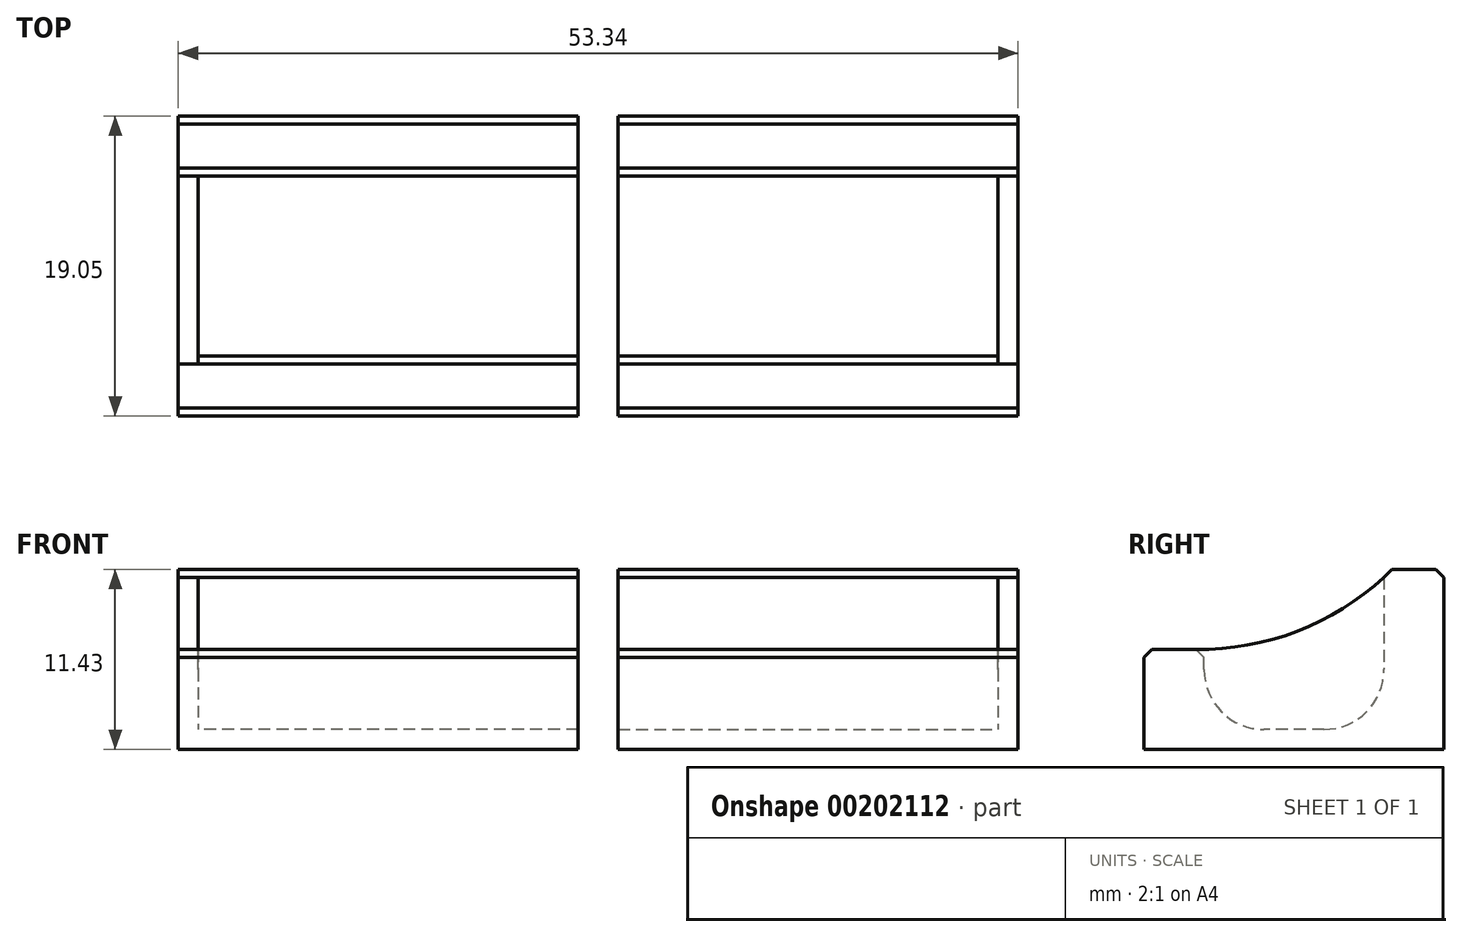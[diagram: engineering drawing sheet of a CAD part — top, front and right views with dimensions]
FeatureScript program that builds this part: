
annotation { "Feature Type Name" : "Feature", "Feature Type Description" : "" }
export const myFeature = defineFeature(function(context is Context, id is Id, definition is map)
    precondition{}
    {
        {
            var Q0;
            Q0=qCreatedBy(makeId("Right.planeOp"),FACE);
            var sketch = newSketch(context, id + "F0", { "sketchPlane" : qUnion([Q0])});
            skLineSegment(sketch, "E0", {"start": v(0, 0) * mm, "end": v(19.05, 0) * mm});
            skLineSegment(sketch, "E1", {"start": v(19.05, 0) * mm, "end": v(19.05, 11.43) * mm});
            skLineSegment(sketch, "E2", {"start": v(19.05, 11.43) * mm, "end": v(15.24, 11.43) * mm});
            skLineSegment(sketch, "E3", {"start": v(15.24, 11.43) * mm, "end": v(15.24, 1.27) * mm});
            skLineSegment(sketch, "E4", {"start": v(15.24, 1.27) * mm, "end": v(3.8, 1.27) * mm});
            skLineSegment(sketch, "E5", {"start": v(3.8, 1.27) * mm, "end": v(3.8, 6.35) * mm});
            skLineSegment(sketch, "E6", {"start": v(3.8, 6.35) * mm, "end": v(0, 6.35) * mm});
            skLineSegment(sketch, "E7", {"start": v(0, 6.35) * mm, "end": v(0, 0) * mm});
            skSolve(sketch);
        }
        {
            var Q0;
            Q0=makeQuery(id+"F0.imprint","IMPRINT",FACE,{"disambiguationData":[TD([[makeQuery(id+"F0.imprint","IMPRINT",EDGE,{"derivedFrom":sQuery(id+"F0.wireOp",EDGE,"E0")}),1.0]])]});
            extrude(context, id + "F1", {"entities" : qUnion([Q0]), "depth" : 25.4 * mm});
        }
        {
            var Q0;
            Q0=makeQuery(id+"F1.opExtrude","SWEPT_EDGE",EDGE,{"disambiguationData":[OSD([sQuery(id+"F0.wireOp",EDGE,"E1"),sQuery(id+"F0.wireOp",EDGE,"E2")])]});
            var Q1;
            Q1=makeQuery(id+"F1.opExtrude","SWEPT_EDGE",EDGE,{"disambiguationData":[OSD([sQuery(id+"F0.wireOp",EDGE,"E6"),sQuery(id+"F0.wireOp",EDGE,"E7")])]});
            chamfer(context, id + "F2", {"entities" : qUnion([Q0, Q1]), "width" : 0.5 * mm, "tangentPropagation" : true});
        }
        {
            var Q0;
            Q0=makeQuery(id+"F1.opExtrude","SWEPT_EDGE",EDGE,{"disambiguationData":[OSD([sQuery(id+"F0.wireOp",EDGE,"E5"),sQuery(id+"F0.wireOp",EDGE,"E6")])]});
            var Q1;
            Q1=makeQuery(id+"F1.opExtrude","SWEPT_EDGE",EDGE,{"disambiguationData":[OSD([sQuery(id+"F0.wireOp",EDGE,"E2"),sQuery(id+"F0.wireOp",EDGE,"E3")])]});
            chamfer(context, id + "F3", {"entities" : qUnion([Q0, Q1]), "width" : 0.5 * mm, "tangentPropagation" : true});
        }
        {
            var Q0;
            Q0=makeQuery(id+"F1.opExtrude","SWEPT_EDGE",EDGE,{"disambiguationData":[OSD([sQuery(id+"F0.wireOp",EDGE,"E3"),sQuery(id+"F0.wireOp",EDGE,"E4")])]});
            var Q1;
            Q1=makeQuery(id+"F1.opExtrude","SWEPT_EDGE",EDGE,{"disambiguationData":[OSD([sQuery(id+"F0.wireOp",EDGE,"E4"),sQuery(id+"F0.wireOp",EDGE,"E5")])]});
            fillet(context, id + "F4", {"entities" : qUnion([Q0, Q1]), "radius" : 3.8 * mm, "tangentPropagation" : true, "allowEdgeOverflow" : false});
        }
        {
            var Q0;
            Q0=qCreatedBy(makeId("Right.planeOp"),FACE);
            var sketch = newSketch(context, id + "F5", { "sketchPlane" : qUnion([Q0])});
            skArc(sketch, "E8", {"start": v(3.3, 6.35) * mm, "mid": v(9.7, 7.5) * mm, "end": v(15.24, 10.92) * mm});
            skLineSegment(sketch, "E9", {"start": v(15.24, 10.92) * mm, "end": v(15.24, 0.52) * mm});
            skLineSegment(sketch, "E10", {"start": v(15.24, 0.52) * mm, "end": v(3.07, 0.52) * mm});
            skLineSegment(sketch, "E11", {"start": v(3.07, 0.52) * mm, "end": v(3.3, 6.35) * mm});
            skSolve(sketch);
        }
        {
            var Q0;
            Q0 = qSketchRegion(id + "F5", true);
            extrude(context, id + "F6", {"entities" : qUnion([Q0]), "operationType" : NewBodyOperationType.ADD, "depth" : 1.27 * mm});
        }
        {
            var Q0;
            Q0=makeQuery(id+"F1.opExtrude","CAP_FACE",FACE,{"disambiguationData":[OSD([sQuery(id+"F0.wireOp",EDGE,"E0"),sQuery(id+"F0.wireOp",EDGE,"E1"),sQuery(id+"F0.wireOp",EDGE,"E2"),sQuery(id+"F0.wireOp",EDGE,"E3"),sQuery(id+"F0.wireOp",EDGE,"E4"),sQuery(id+"F0.wireOp",EDGE,"E5"),sQuery(id+"F0.wireOp",EDGE,"E6"),sQuery(id+"F0.wireOp",EDGE,"E7")])],"isStart":false});
            cPlane(context, id + "F7", {"entities" : qUnion([Q0]), "cplaneType" : CPlaneType.OFFSET, "offset" : 1.27 * mm, "width" : 152.4 * mm, "height" : 152.4 * mm});
        }
        {
            var Q0;
            Q0=makeQuery(id+"F1.opExtrude","SWEPT_BODY",BODY,{"disambiguationData":[OSD([sQuery(id+"F0.wireOp",EDGE,"E0"),sQuery(id+"F0.wireOp",EDGE,"E1"),sQuery(id+"F0.wireOp",EDGE,"E2"),sQuery(id+"F0.wireOp",EDGE,"E3"),sQuery(id+"F0.wireOp",EDGE,"E4"),sQuery(id+"F0.wireOp",EDGE,"E5"),sQuery(id+"F0.wireOp",EDGE,"E6"),sQuery(id+"F0.wireOp",EDGE,"E7")])]});
            var Q1;
            Q1=qCreatedBy(id+"F7.planeOp",FACE);
            mirror(context, id + "F8", {"entities" : qUnion([Q0]), "mirrorPlane" : qUnion([Q1])});
        }
    });
